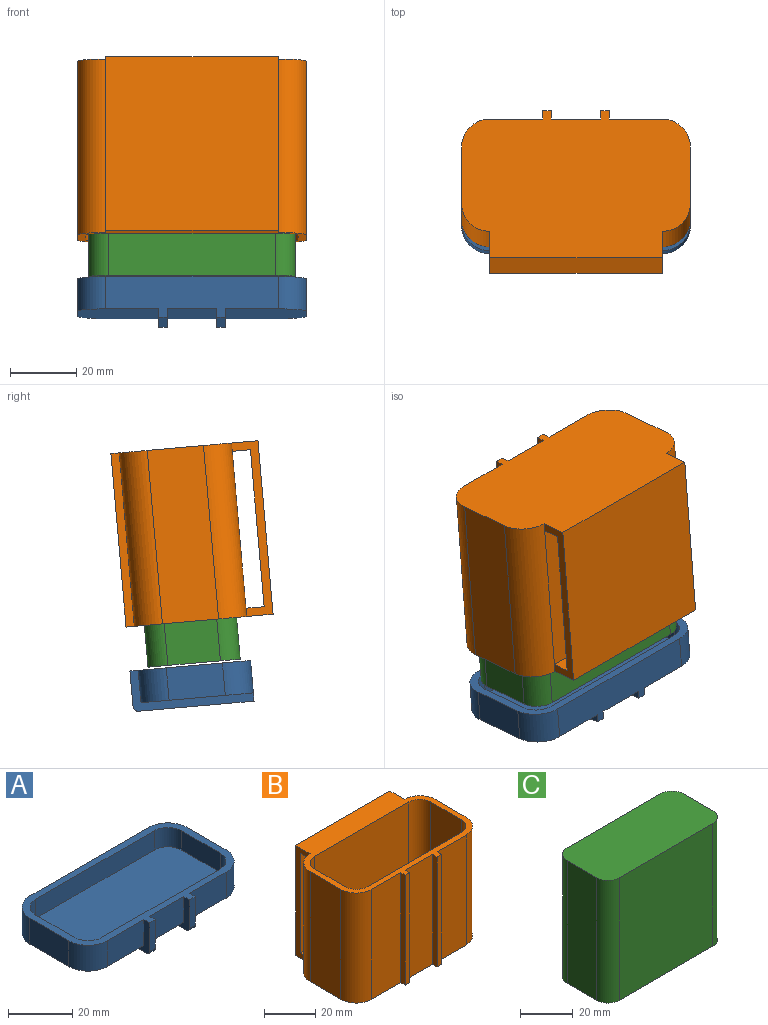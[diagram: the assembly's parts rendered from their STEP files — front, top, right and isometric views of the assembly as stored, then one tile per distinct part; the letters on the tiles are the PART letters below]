
ASSEMBLY  parts=3 mates=2
PART A: 33 faces, bbox 69x36.5x12.3 mm
  f0: plane 16x9.8mm, normal (0,-1,0), area 156.8mm2, adj f7,f12,f13,f27
  f1: plane 15x9.8mm, normal (0,-1,0), area 147mm2, adj f2,f12,f23,f26
  f2: plane 34x15mm, normal (0,0,-1), area 510mm2, adj f1,f10,f23,f26
  f3: plane 34x24.5mm, normal (0,0,-1), area 802mm2, adj f4,f5,f6,f10,f11,f24
  f4: plane 17x9.8mm, normal (-1,0,0), area 166.6mm2, adj f3,f5,f11,f12
  f5: cylinder r=8.5mm len=9.8mm, axis (0,0,-1), area 130.8mm2, adj f3,f4,f6,f12
  f6: plane 16x9.8mm, normal (0,-1,0), area 156.8mm2, adj f3,f5,f12,f24
  f7: cylinder r=8.5mm len=9.8mm, axis (0,0,-1), area 130.8mm2, adj f0,f8,f12,f13
  f8: plane 17x9.8mm, normal (1,0,0), area 166.6mm2, adj f7,f9,f12,f13
  f9: cylinder r=8.5mm len=9.8mm, axis (0,0,-1), area 130.8mm2, adj f8,f10,f12,f13
  f10: plane 52x12.3mm, normal (0,1,0), area 522.1mm2, adj f2,f3,f9,f11,f12,f13,f23,f24
  f11: cylinder r=8.5mm len=9.8mm, axis (0,0,-1), area 130.8mm2, adj f3,f4,f10,f12
  f12: plane 69x36.5mm, normal (0,0,1), area 471.4mm2, adj f0,f1,f4,f5,f6,f7,f8,f9
  f13: plane 34x24.5mm, normal (0,0,-1), area 802mm2, adj f0,f7,f8,f9,f10,f27
  f14: plane 17x7.3mm, normal (1,0,0), area 124.1mm2, adj f12,f15,f21,f22
  f15: cylinder r=6mm len=7.3mm, axis (0,0,-1), area 68.8mm2, adj f12,f14,f16,f22
  f16: plane 52x7.3mm, normal (0,1,0), area 379.6mm2, adj f12,f15,f17,f22
  f17: cylinder r=6mm len=7.3mm, axis (0,0,-1), area 68.8mm2, adj f12,f16,f18,f22
  f18: plane 17x7.3mm, normal (-1,0,0), area 124.1mm2, adj f12,f17,f19,f22
  f19: cylinder r=6mm len=7.3mm, axis (0,0,-1), area 68.8mm2, adj f12,f18,f20,f22
  f20: plane 52x7.3mm, normal (0,-1,0), area 379.6mm2, adj f12,f19,f21,f22
  f21: cylinder r=6mm len=7.3mm, axis (0,0,-1), area 68.8mm2, adj f12,f14,f20,f22
  f22: plane 64x29mm, normal (0,0,1), area 1825.1mm2, adj f14,f15,f16,f17,f18,f19,f20,f21
  f23: plane 36.5x12.3mm, normal (1,0,0), area 115.3mm2, adj f1,f2,f10,f12,f25,f29,f32
  f24: plane 36.5x12.3mm, normal (-1,0,0), area 115.3mm2, adj f3,f6,f10,f12,f25,f29,f32
  f25: plane 35x2.5mm, normal (0,0,-1), area 87.5mm2, adj f10,f23,f24,f32
  f26: plane 36.5x12.3mm, normal (-1,0,0), area 115.3mm2, adj f1,f2,f10,f12,f28,f30,f31
  f27: plane 36.5x12.3mm, normal (1,0,0), area 115.3mm2, adj f0,f10,f12,f13,f28,f30,f31
  f28: plane 35x2.5mm, normal (0,0,-1), area 87.5mm2, adj f10,f26,f27,f31
  f29: plane 10.8x2.5mm, normal (0,-1,0), area 27mm2, adj f12,f23,f24,f32
  f30: plane 10.8x2.5mm, normal (0,-1,0), area 27mm2, adj f12,f26,f27,f31
  f31: cylinder r=1.5mm len=2.5mm, axis (1,0,0), area 5.9mm2, adj f26,f27,f28,f30
  f32: cylinder r=1.5mm len=2.5mm, axis (1,0,0), area 5.9mm2, adj f23,f24,f25,f29
PART B: 33 faces, bbox 69x44.5x52.5 mm
  f0: plane 52.5x8mm, normal (-1,0,0), area 158.8mm2, adj f9,f10,f11,f28,f30,f31,f32
  f1: plane 52.5x15mm, normal (0,-1,0), area 787.5mm2, adj f10,f11,f21,f24
  f2: plane 52.5x16mm, normal (0,-1,0), area 840mm2, adj f4,f10,f11,f22
  f3: plane 52.5x17mm, normal (-1,0,0), area 892.5mm2, adj f4,f9,f10,f11
  f4: cylinder r=8.5mm len=52.5mm, axis (0,0,-1), area 701mm2, adj f2,f3,f10,f11
  f5: plane 52.5x16mm, normal (0,-1,0), area 840mm2, adj f6,f10,f11,f25
  f6: cylinder r=8.5mm len=52.5mm, axis (0,0,-1), area 701mm2, adj f5,f7,f10,f11
  f7: plane 52.5x17mm, normal (1,0,0), area 892.5mm2, adj f6,f8,f10,f11
  f8: cylinder r=8.5mm len=52.5mm, axis (0,0,-1), area 701mm2, adj f7,f10,f11,f27,f29
  f9: cylinder r=8.5mm len=52.5mm, axis (0,0,-1), area 701mm2, adj f0,f3,f10,f11,f29
  f10: plane 69x44.5mm, normal (0,0,1), area 887.4mm2, adj f0,f1,f2,f3,f4,f5,f6,f7
  f11: plane 69x44.5mm, normal (0,0,-1), area 2712.5mm2, adj f0,f1,f2,f3,f4,f5,f6,f7
  f12: plane 50x17mm, normal (1,0,0), area 850mm2, adj f10,f13,f19,f20
  f13: cylinder r=6mm len=50mm, axis (0,0,-1), area 471.2mm2, adj f10,f12,f14,f20
  f14: plane 52x50mm, normal (0,1,0), area 2600mm2, adj f10,f13,f15,f20
  f15: cylinder r=6mm len=50mm, axis (0,0,-1), area 471.2mm2, adj f10,f14,f16,f20
  f16: plane 50x17mm, normal (-1,0,0), area 850mm2, adj f10,f15,f17,f20
  f17: cylinder r=6mm len=50mm, axis (0,0,-1), area 471.2mm2, adj f10,f16,f18,f20
  f18: plane 52x50mm, normal (0,-1,0), area 2600mm2, adj f10,f17,f19,f20
  f19: cylinder r=6mm len=50mm, axis (0,0,-1), area 471.2mm2, adj f10,f12,f18,f20
  f20: plane 64x29mm, normal (0,0,1), area 1825.1mm2, adj f12,f13,f14,f15,f16,f17,f18,f19
  f21: plane 52.5x2.5mm, normal (1,0,0), area 131.2mm2, adj f1,f10,f11,f23
  f22: plane 52.5x2.5mm, normal (-1,0,0), area 131.2mm2, adj f2,f10,f11,f23
  f23: plane 52.5x2.5mm, normal (0,-1,0), area 131.2mm2, adj f10,f11,f21,f22
  f24: plane 52.5x2.5mm, normal (-1,0,0), area 131.2mm2, adj f1,f10,f11,f26
  f25: plane 52.5x2.5mm, normal (1,0,0), area 131.2mm2, adj f5,f10,f11,f26
  f26: plane 52.5x2.5mm, normal (0,-1,0), area 131.2mm2, adj f10,f11,f24,f25
  f27: plane 52.5x8mm, normal (1,0,0), area 158.8mm2, adj f8,f10,f11,f28,f30,f31,f32
  f28: plane 52.5x52mm, normal (0,1,0), area 2730mm2, adj f0,f10,f11,f27
  f29: plane 52x47.5mm, normal (0,1,0), area 2470mm2, adj f8,f9,f30,f31
  f30: plane 52x5.5mm, normal (0,0,-1), area 286mm2, adj f0,f27,f29,f32
  f31: plane 52x5.5mm, normal (0,0,1), area 286mm2, adj f0,f27,f29,f32
  f32: plane 52x47.5mm, normal (0,-1,0), area 2470mm2, adj f0,f27,f30,f31
PART C: 10 faces, bbox 62.4x27.9x57 mm
  f0: plane 57x15.9mm, normal (-1,0,0), area 906.3mm2, adj f1,f7,f8,f9
  f1: cylinder r=6mm len=57mm, axis (0,0,-1), area 537.2mm2, adj f0,f2,f8,f9
  f2: plane 57x50.4mm, normal (0,-1,0), area 2872.8mm2, adj f1,f3,f8,f9
  f3: cylinder r=6mm len=57mm, axis (0,0,-1), area 537.2mm2, adj f2,f4,f8,f9
  f4: plane 57x15.9mm, normal (1,0,0), area 906.3mm2, adj f3,f5,f8,f9
  f5: cylinder r=6mm len=57mm, axis (0,0,-1), area 537.2mm2, adj f4,f6,f8,f9
  f6: plane 57x50.4mm, normal (0,1,0), area 2872.8mm2, adj f5,f7,f8,f9
  f7: cylinder r=6mm len=57mm, axis (0,0,-1), area 537.2mm2, adj f0,f6,f8,f9
  f8: plane 62.4x27.9mm, normal (0,0,1), area 1710.1mm2, adj f0,f1,f2,f3,f4,f5,f6,f7
  f9: plane 62.4x27.9mm, normal (0,0,-1), area 1710.1mm2, adj f0,f1,f2,f3,f4,f5,f6,f7
PLACE A rot(axis=(0,0.04,1),180deg) t=(-68.06,-57.03,43.42)mm
PLACE B rot(axis=(1,0,0),175deg) t=(-48.07,-50.88,113.76)mm
PLACE C rot(axis=(1,0,0),175deg) t=(-47.27,-48.93,107.95)mm
MATE slider C.f9 <-> B.f20  axis (0,0.09,1) through (-58.07,-39.85,107.15)mm
MATE slider C.f8 <-> A.f22  axis (0,-0.09,-1) through (-58.07,-44.81,50.37)mm
